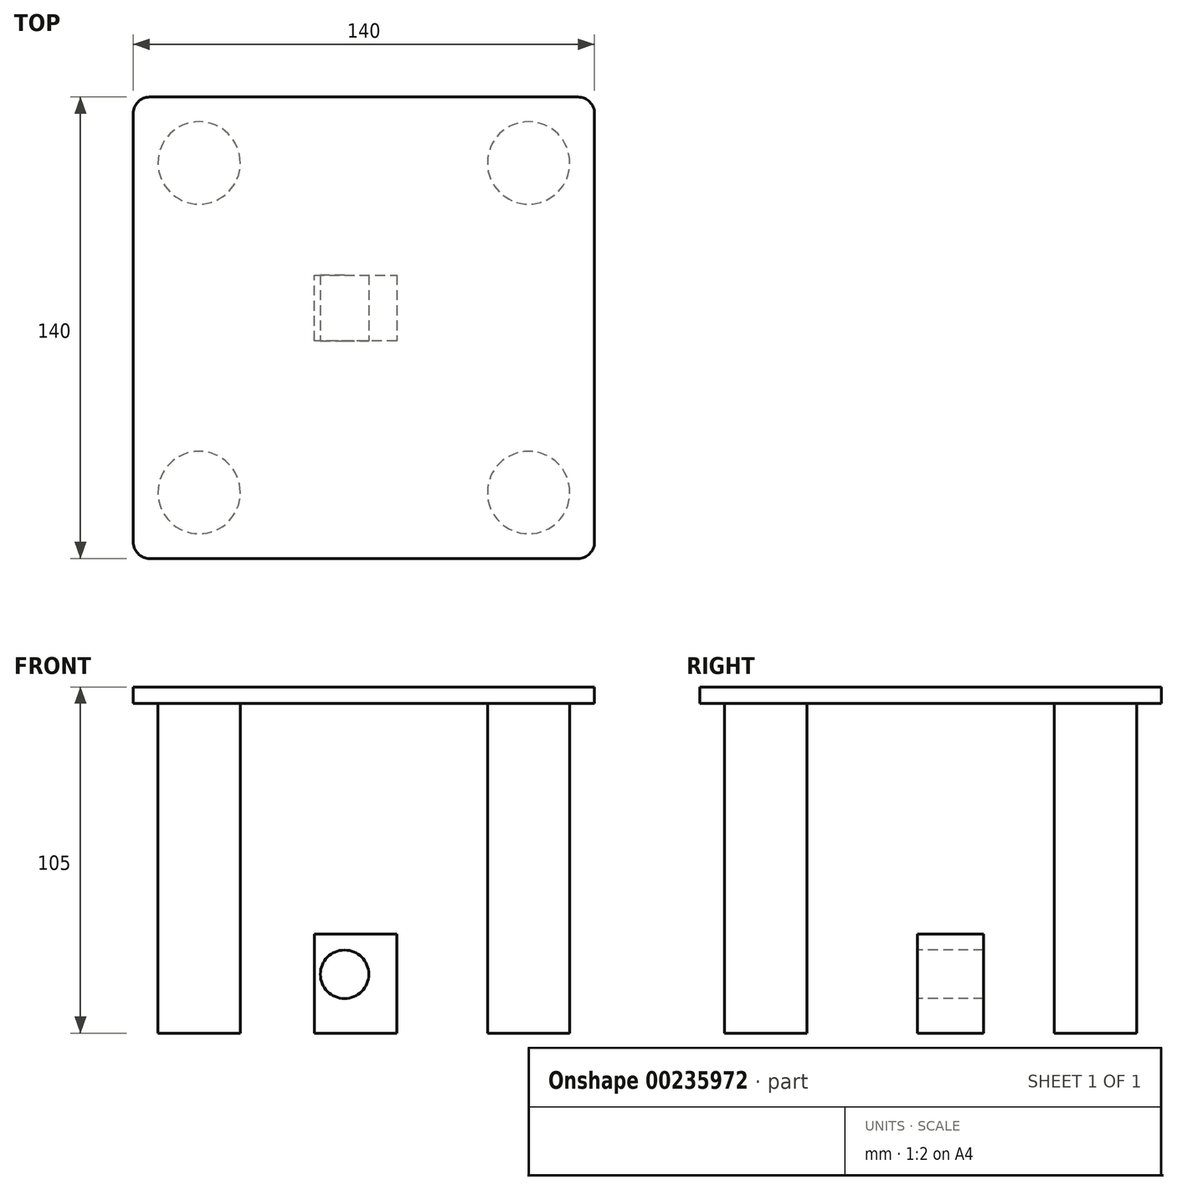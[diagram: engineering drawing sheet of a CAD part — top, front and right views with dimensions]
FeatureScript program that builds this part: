
annotation { "Feature Type Name" : "Feature", "Feature Type Description" : "" }
export const myFeature = defineFeature(function(context is Context, id is Id, definition is map)
    precondition{}
    {
        {
            var Q0;
            Q0=qCreatedBy(makeId("Top.planeOp"),FACE);
            var sketch = newSketch(context, id + "F0", { "sketchPlane" : qUnion([Q0])});
            skLineSegment(sketch, "E0", {"start": v(-15, -4) * mm, "end": v(-15, 16) * mm});
            skLineSegment(sketch, "E1", {"start": v(-15, 16) * mm, "end": v(10, 16) * mm});
            skLineSegment(sketch, "E2", {"start": v(10, 16) * mm, "end": v(10, -4) * mm});
            skLineSegment(sketch, "E3", {"start": v(10, -4) * mm, "end": v(-15, -4) * mm});
            skSolve(sketch);
        }
        {
            var Q0;
            Q0 = qSketchRegion(id + "F0", true);
            extrude(context, id + "F1", {"entities" : qUnion([Q0]), "depth" : 30 * mm});
        }
        {
            var Q0;
            Q0=makeQuery(id+"F1.opExtrude","SWEPT_FACE",FACE,{"disambiguationData":[OSD([sQuery(id+"F0.wireOp",EDGE,"E3")])]});
            var sketch = newSketch(context, id + "F2", { "sketchPlane" : qUnion([Q0])});
            skCircle(sketch, "E4", {"center": v(-5.86, 17.85) * mm, "radius": 7.34 * mm});
            skSolve(sketch);
        }
        {
            var Q0;
            Q0 = qSketchRegion(id + "F2", true);
            extrude(context, id + "F3", {"entities" : qUnion([Q0]), "operationType" : NewBodyOperationType.REMOVE, "endBound" : BoundingType.UP_TO_NEXT, "oppositeDirection" : true, "depth" : 25 * mm});
        }
        {
            var Q0;
            Q0=qCreatedBy(makeId("Top.planeOp"),FACE);
            var sketch = newSketch(context, id + "F4", { "sketchPlane" : qUnion([Q0])});
            skCircle(sketch, "E5", {"center": v(-50, -50) * mm, "radius": 12.5 * mm});
            skCircle(sketch, "E6.0.1.0", {"center": v(-50, 50) * mm, "radius": 12.5 * mm});
            skCircle(sketch, "E6.1.0.0", {"center": v(50, -50) * mm, "radius": 12.5 * mm});
            skCircle(sketch, "E6.1.1.0", {"center": v(50, 50) * mm, "radius": 12.5 * mm});
            skLineSegment(sketch, "E6.direction1", {"start": v(-50, -50) * mm, "end": v(50, -50) * mm, "construction": true});
            skLineSegment(sketch, "E6.direction2", {"start": v(-50, -50) * mm, "end": v(-50, 50) * mm, "construction": true});
            skSolve(sketch);
        }
        {
            var Q0;
            Q0=makeQuery(id+"F4.imprint","IMPRINT",FACE,{"disambiguationData":[TD([[makeQuery(id+"F4.imprint","IMPRINT",EDGE,{"derivedFrom":sQuery(id+"F4.wireOp",EDGE,"E5")}),1.0]])]});
            var Q1;
            Q1=makeQuery(id+"F4.imprint","IMPRINT",FACE,{"disambiguationData":[TD([[makeQuery(id+"F4.imprint","IMPRINT",EDGE,{"derivedFrom":sQuery(id+"F4.wireOp",EDGE,"E6.0.1.0")}),1.0]])]});
            var Q2;
            Q2=makeQuery(id+"F4.imprint","IMPRINT",FACE,{"disambiguationData":[TD([[makeQuery(id+"F4.imprint","IMPRINT",EDGE,{"derivedFrom":sQuery(id+"F4.wireOp",EDGE,"E6.1.1.0")}),1.0]])]});
            var Q3;
            Q3=makeQuery(id+"F4.imprint","IMPRINT",FACE,{"disambiguationData":[TD([[makeQuery(id+"F4.imprint","IMPRINT",EDGE,{"derivedFrom":sQuery(id+"F4.wireOp",EDGE,"E6.1.0.0")}),1.0]])]});
            extrude(context, id + "F5", {"entities" : qUnion([Q0, Q1, Q2, Q3]), "depth" : 100 * mm});
        }
        {
            var Q0;
            Q0=makeQuery(id+"F5.opExtrude","CAP_FACE",FACE,{"disambiguationData":[OSD([sQuery(id+"F4.wireOp",EDGE,"E6.0.1.0")])],"isStart":false});
            var sketch = newSketch(context, id + "F6", { "sketchPlane" : qUnion([Q0])});
            skLineSegment(sketch, "E7.bottom", {"start": v(-70, 70) * mm, "end": v(70, 70) * mm});
            skLineSegment(sketch, "E7.top", {"start": v(-70, -70) * mm, "end": v(70, -70) * mm});
            skLineSegment(sketch, "E7.left", {"start": v(-70, 70) * mm, "end": v(-70, -70) * mm});
            skLineSegment(sketch, "E7.right", {"start": v(70, 70) * mm, "end": v(70, -70) * mm});
            skCircle(sketch, "E8.0", {"center": v(-50, 50) * mm, "radius": 12.5 * mm, "construction": true});
            skCircle(sketch, "E9.0", {"center": v(50, 50) * mm, "radius": 12.5 * mm, "construction": true});
            skCircle(sketch, "E10.0", {"center": v(50, -50) * mm, "radius": 12.5 * mm, "construction": true});
            skCircle(sketch, "E11.0", {"center": v(-50, -50) * mm, "radius": 12.5 * mm, "construction": true});
            skSolve(sketch);
        }
        {
            var Q0;
            Q0 = qSketchRegion(id + "F6", true);
            extrude(context, id + "F7", {"entities" : qUnion([Q0]), "depth" : 5 * mm});
        }
        {
            var Q0;
            Q0=makeQuery(id+"F7.opExtrude","SWEPT_EDGE",EDGE,{"disambiguationData":[OSD([sQuery(id+"F6.wireOp",EDGE,"E7.top"),sQuery(id+"F6.wireOp",EDGE,"E7.left")])]});
            var Q1;
            Q1=makeQuery(id+"F7.opExtrude","SWEPT_EDGE",EDGE,{"disambiguationData":[OSD([sQuery(id+"F6.wireOp",EDGE,"E7.top"),sQuery(id+"F6.wireOp",EDGE,"E7.right")])]});
            var Q2;
            Q2=makeQuery(id+"F7.opExtrude","SWEPT_EDGE",EDGE,{"disambiguationData":[OSD([sQuery(id+"F6.wireOp",EDGE,"E7.bottom"),sQuery(id+"F6.wireOp",EDGE,"E7.right")])]});
            var Q3;
            Q3=makeQuery(id+"F7.opExtrude","SWEPT_EDGE",EDGE,{"disambiguationData":[OSD([sQuery(id+"F6.wireOp",EDGE,"E7.bottom"),sQuery(id+"F6.wireOp",EDGE,"E7.left")])]});
            fillet(context, id + "F8", {"entities" : qUnion([Q0, Q1, Q2, Q3]), "radius" : 5 * mm, "tangentPropagation" : true, "allowEdgeOverflow" : false});
        }
    });
